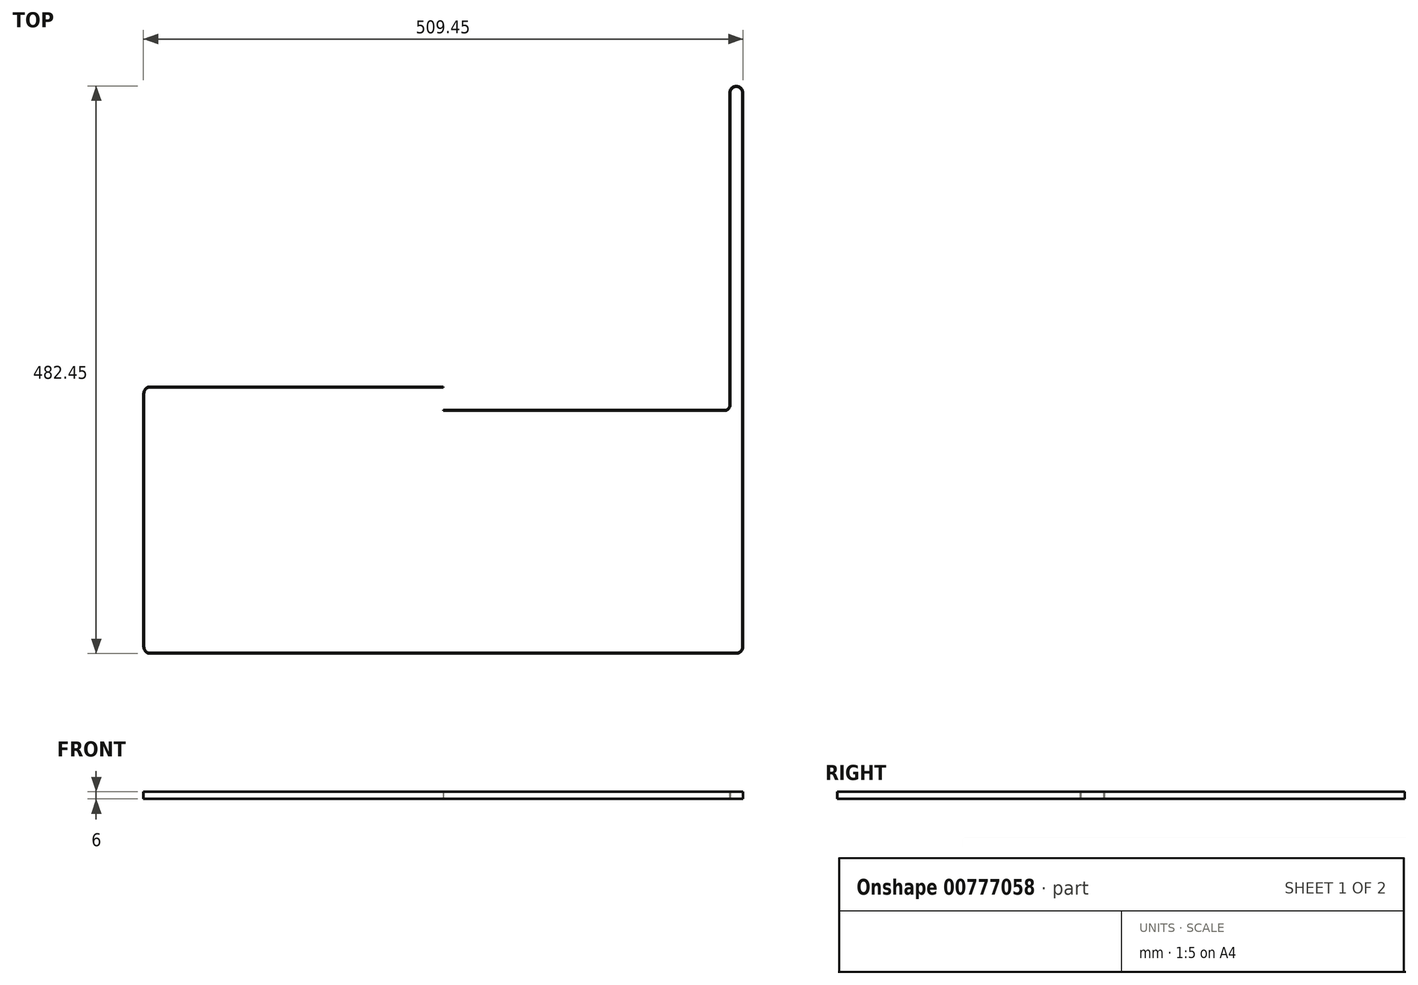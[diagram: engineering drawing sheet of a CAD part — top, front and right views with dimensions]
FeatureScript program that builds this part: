
annotation { "Feature Type Name" : "Feature", "Feature Type Description" : "" }
export const myFeature = defineFeature(function(context is Context, id is Id, definition is map)
    precondition{}
    {
        {
            var Q0;
            Q0=qCreatedBy(makeId("Top.planeOp"),FACE);
            var sketch = newSketch(context, id + "F0", { "sketchPlane" : qUnion([Q0])});
            skLineSegment(sketch, "E0", {"start": v(254.1, 260.5) * mm, "end": v(254.1, -210.5) * mm});
            skLineSegment(sketch, "E1", {"start": v(249, -215.6) * mm, "end": v(0, -215.6) * mm});
            skArc(sketch, "E2", {"start": v(254.1, 260.5) * mm, "mid": v(249, 265.6) * mm, "end": v(243.9, 260.5) * mm});
            skLineSegment(sketch, "E3", {"start": v(243.9, 260.5) * mm, "end": v(243.9, -5) * mm});
            skArc(sketch, "E4", {"start": v(249, -215.6) * mm, "mid": v(252.6, -214.1) * mm, "end": v(254.1, -210.5) * mm});
            skArc(sketch, "E5", {"start": v(239.05, -9.22) * mm, "mid": v(242.04, -7.99) * mm, "end": v(243.28, -5) * mm});
            skLineSegment(sketch, "E6", {"start": v(239.05, -9.22) * mm, "end": v(0, -9.22) * mm});
            skArc(sketch, "E7", {"start": v(254.72, 260.5) * mm, "mid": v(249, 266.22) * mm, "end": v(243.27, 260.5) * mm});
            skArc(sketch, "E8", {"start": v(239.05, -9.85) * mm, "mid": v(242.48, -8.43) * mm, "end": v(243.9, -5) * mm});
            skArc(sketch, "E9", {"start": v(249, -216.22) * mm, "mid": v(253.05, -214.55) * mm, "end": v(254.73, -210.5) * mm});
            skLineSegment(sketch, "E10", {"start": v(254.72, 260.5) * mm, "end": v(254.73, -210.5) * mm});
            skLineSegment(sketch, "E11", {"start": v(0, -216.22) * mm, "end": v(249, -216.22) * mm});
            skLineSegment(sketch, "E12", {"start": v(236.66, -9.22) * mm, "end": v(0, -9.22) * mm});
            skLineSegment(sketch, "E13", {"start": v(243.27, 260.5) * mm, "end": v(243.27, -5) * mm});
            skLineSegment(sketch, "E14", {"start": v(239.05, -9.85) * mm, "end": v(0, -9.85) * mm});
            skArc(sketch, "E15.MirrorCS", {"start": v(-249, -215.6) * mm, "mid": v(-252.6, -214.1) * mm, "end": v(-254.1, -210.5) * mm});
            skArc(sketch, "E16.MirrorCS", {"start": v(-249, -216.22) * mm, "mid": v(-253.05, -214.55) * mm, "end": v(-254.73, -210.5) * mm});
            skLineSegment(sketch, "E17.MirrorCS", {"start": v(-249, -215.6) * mm, "end": v(0, -215.6) * mm});
            skLineSegment(sketch, "E18.MirrorCS", {"start": v(-254.72, 5) * mm, "end": v(-254.73, -210.5) * mm});
            skLineSegment(sketch, "E19.MirrorCS", {"start": v(0, -216.23) * mm, "end": v(-249, -216.23) * mm});
            skLineSegment(sketch, "E20.MirrorCS", {"start": v(-254.1, 5) * mm, "end": v(-254.1, -210.5) * mm});
            skArc(sketch, "E21", {"start": v(-249, 10.1) * mm, "mid": v(-252.6, 8.6) * mm, "end": v(-254.1, 5) * mm});
            skLineSegment(sketch, "E22", {"start": v(0, 10.12) * mm, "end": v(0, 10.1) * mm});
            skLineSegment(sketch, "E23", {"start": v(0, 10.1) * mm, "end": v(-249, 10.1) * mm});
            skPoint(sketch, "E24.orphan", {"position": v(0, -9.22) * mm});
            skPoint(sketch, "E25.MirrorCS.end.orphan", {"position": v(0, -9.85) * mm});
            skLineSegment(sketch, "E26", {"start": v(0, -9.85) * mm, "end": v(0, -9.22) * mm});
            skLineSegment(sketch, "E27", {"start": v(-249, 10.72) * mm, "end": v(0, 10.73) * mm});
            skLineSegment(sketch, "E28", {"start": v(0, 10.73) * mm, "end": v(0, 10.12) * mm});
            skArc(sketch, "E29", {"start": v(-249, 10.72) * mm, "mid": v(-253.05, 9.05) * mm, "end": v(-254.72, 5) * mm});
            skSolve(sketch);
        }
        {
            var Q0;
            Q0=qSketchRegion(id+"F0",true);
            extrude(context, id + "F1", {"entities" : qUnion([Q0]), "depth" : 6 * mm, "offsetDistance" : 25 * mm});
        }
    });
